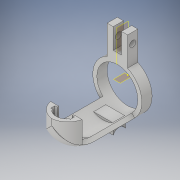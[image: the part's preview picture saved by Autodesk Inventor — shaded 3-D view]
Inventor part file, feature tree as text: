
AUTODESK INVENTOR PART (.ipt)
format: ipt  version: 2018 (Build 220112000, 112)  size: 248,320 bytes
history: native  units: in
note: dims shown in document units (in); Inventor stores cm internally (conversion verified against a paired STEP export)
features: sketch x10, extrude x8, plane x2, revolve x1, mirror x1
ambient origin geometry x8: Origin, YZ Plane, XZ Plane, XY Plane, X Axis, Y Axis, Z Axis, Center Point
bodies: Solid1 (feature_tree)
feature tree (22):
  extrude  "Extrusion1"  Depth=0.0787in
  extrude  "Extrusion3"  Depth=0.9449in
  extrude  "Extrusion4"  Depth=0.7874in
  plane  "Work Plane1"
  revolve  "Revolution1"  [1 undecoded]
  plane  "Work Plane2"
  extrude  "Extrusion6"  Depth=0.3937in TaperAngle=0.0deg
  sketch  "Sketch9"  dims[d36=-0.1969in d45=90.0deg]
  extrude  "Extrusion7"  TaperAngle=90.0deg  [1 undecoded]
  extrude  "Extrusion8"  [1 undecoded]
  mirror  "Mirror1"
  extrude  "Extrusion9"  Depth=0.3937in TaperAngle=0.0deg
  extrude  "Extrusion10"  Depth=0.0787in
  sketch  "Sketch1"  dims[d1=0.6299in d4=0.0787in]
  sketch  "Sketch3"  dims[d16=0.1969in d17=0.0in d23=0.9449in]
  sketch  "Sketch4"  dims[d24=0.7874in d26=0.7874in]
  sketch  "Sketch7"  dims[d27=0.1969in d28=0.0in d30=0.1969in]
  sketch  "Sketch8"  dims[d31=0.1181in d32=0.3937in d33=0.0in]
  sketch  "Sketch10"  dims[d46=0.0591in d47=-0.4724in]
  sketch  "Sketch11"  dims[d49=0.1969in d50=0.3937in d51=0.0in]
  sketch  "Sketch12"  dims[d52=0.0886in d53=0.0787in]
  sketch  "Sketch13"  dims[d54=0.1969in d55=0.0in d56=0.0787in d57=0.0295in d58=-0.2061in d59=0.2362in d61=0.0787in d63=0.3937in d64=0.0in d65=0.1575in d66=0.3937in d67=0.0in d68=0.0984in]
note: 3 required parameter values undecoded (feature->parameter linkage not recoverable at this tier; creation-order binding heuristic only, values carry confidence <= 0.55)